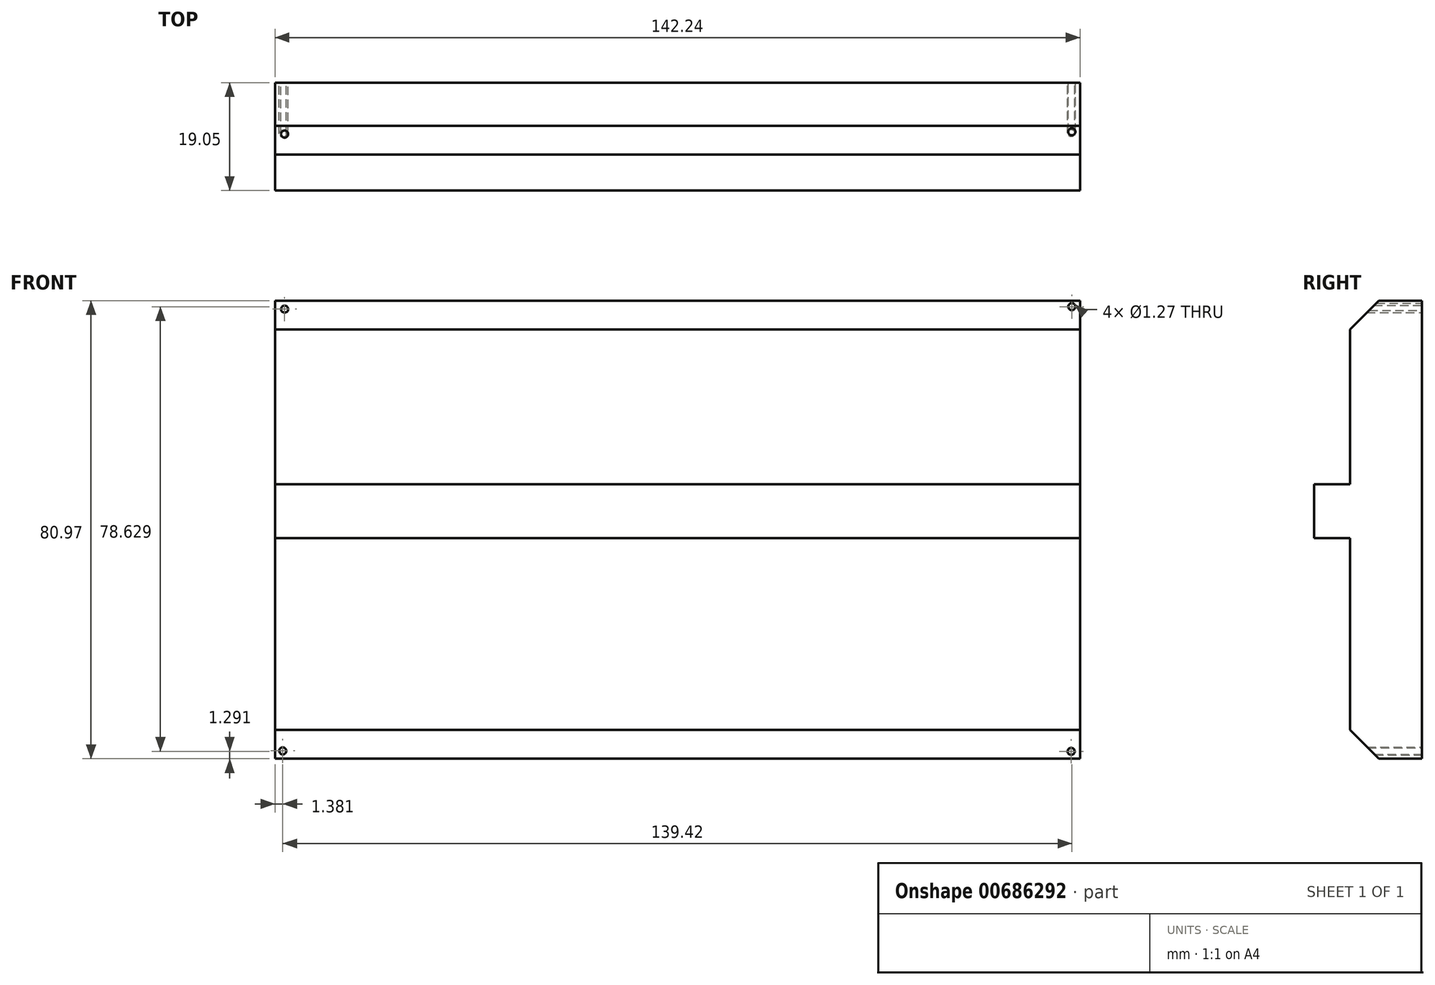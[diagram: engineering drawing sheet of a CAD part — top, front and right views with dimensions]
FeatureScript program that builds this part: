
annotation { "Feature Type Name" : "Feature", "Feature Type Description" : "" }
export const myFeature = defineFeature(function(context is Context, id is Id, definition is map)
    precondition{}
    {
        {
            var Q0;
            Q0=qCreatedBy(makeId("Front.planeOp"),FACE);
            var sketch = newSketch(context, id + "F0", { "sketchPlane" : qUnion([Q0])});
            skLineSegment(sketch, "E0.bottom", {"start": v(-60.47, 58.75) * mm, "end": v(81.77, 58.75) * mm});
            skLineSegment(sketch, "E0.top", {"start": v(-60.47, -22.22) * mm, "end": v(81.77, -22.22) * mm});
            skLineSegment(sketch, "E0.left", {"start": v(-60.47, 58.75) * mm, "end": v(-60.47, -22.22) * mm});
            skLineSegment(sketch, "E0.right", {"start": v(81.77, 58.75) * mm, "end": v(81.77, -22.22) * mm});
            skCircle(sketch, "E1", {"center": v(80.33, 57.7) * mm, "radius": 0.64 * mm});
            skCircle(sketch, "E2", {"center": v(-58.76, 57.27) * mm, "radius": 0.64 * mm});
            skCircle(sketch, "E3", {"center": v(-59.09, -20.84) * mm, "radius": 0.64 * mm});
            skCircle(sketch, "E4", {"center": v(80.22, -20.93) * mm, "radius": 0.64 * mm});
            skSolve(sketch);
        }
        {
            var Q0;
            Q0=makeQuery(id+"F0.imprint","IMPRINT",FACE,{"disambiguationData":[TD([[makeQuery(id+"F0.imprint","IMPRINT",EDGE,{"derivedFrom":sQuery(id+"F0.wireOp",EDGE,"E0.bottom")}),-1.0]])]});
            extrude(context, id + "F1", {"entities" : qUnion([Q0]), "endBound" : BoundingType.SYMMETRIC, "depth" : 12.7 * mm, "offsetDistance" : 25.4 * mm});
        }
        {
            var Q0;
            Q0=makeQuery(id+"F1.opExtrude","CAP_EDGE",EDGE,{"disambiguationData":[OSD([sQuery(id+"F0.wireOp",EDGE,"E0.top")])],"isStart":false});
            var Q1;
            Q1=makeQuery(id+"F1.opExtrude","CAP_EDGE",EDGE,{"disambiguationData":[OSD([sQuery(id+"F0.wireOp",EDGE,"E0.bottom")])],"isStart":false});
            chamfer(context, id + "F2", {"entities" : qUnion([Q0, Q1]), "width" : 5.08 * mm, "tangentPropagation" : true});
        }
        {
            var Q0;
            Q0=makeQuery(id+"F1.opExtrude","CAP_FACE",FACE,{"disambiguationData":[OSD([sQuery(id+"F0.wireOp",EDGE,"E0.bottom"),sQuery(id+"F0.wireOp",EDGE,"E0.top"),sQuery(id+"F0.wireOp",EDGE,"E0.left"),sQuery(id+"F0.wireOp",EDGE,"E0.right")])],"isStart":false});
            var sketch = newSketch(context, id + "F3", { "sketchPlane" : qUnion([Q0])});
            skLineSegment(sketch, "E5.bottom", {"start": v(-60.47, 16.8) * mm, "end": v(81.77, 16.8) * mm});
            skLineSegment(sketch, "E5.top", {"start": v(-60.47, 26.33) * mm, "end": v(81.77, 26.33) * mm});
            skLineSegment(sketch, "E5.left", {"start": v(-60.47, 16.8) * mm, "end": v(-60.47, 26.33) * mm});
            skLineSegment(sketch, "E5.right", {"start": v(81.77, 16.8) * mm, "end": v(81.77, 26.33) * mm});
            skSolve(sketch);
        }
        {
            var Q0;
            Q0=makeQuery(id+"F3.imprint","IMPRINT",FACE,{"disambiguationData":[TD([[makeQuery(id+"F3.imprint","IMPRINT",EDGE,{"derivedFrom":sQuery(id+"F3.wireOp",EDGE,"E5.bottom")}),1.0]])]});
            extrude(context, id + "F4", {"entities" : qUnion([Q0]), "operationType" : NewBodyOperationType.ADD, "depth" : 6.35 * mm, "offsetDistance" : 25.4 * mm});
        }
    });
